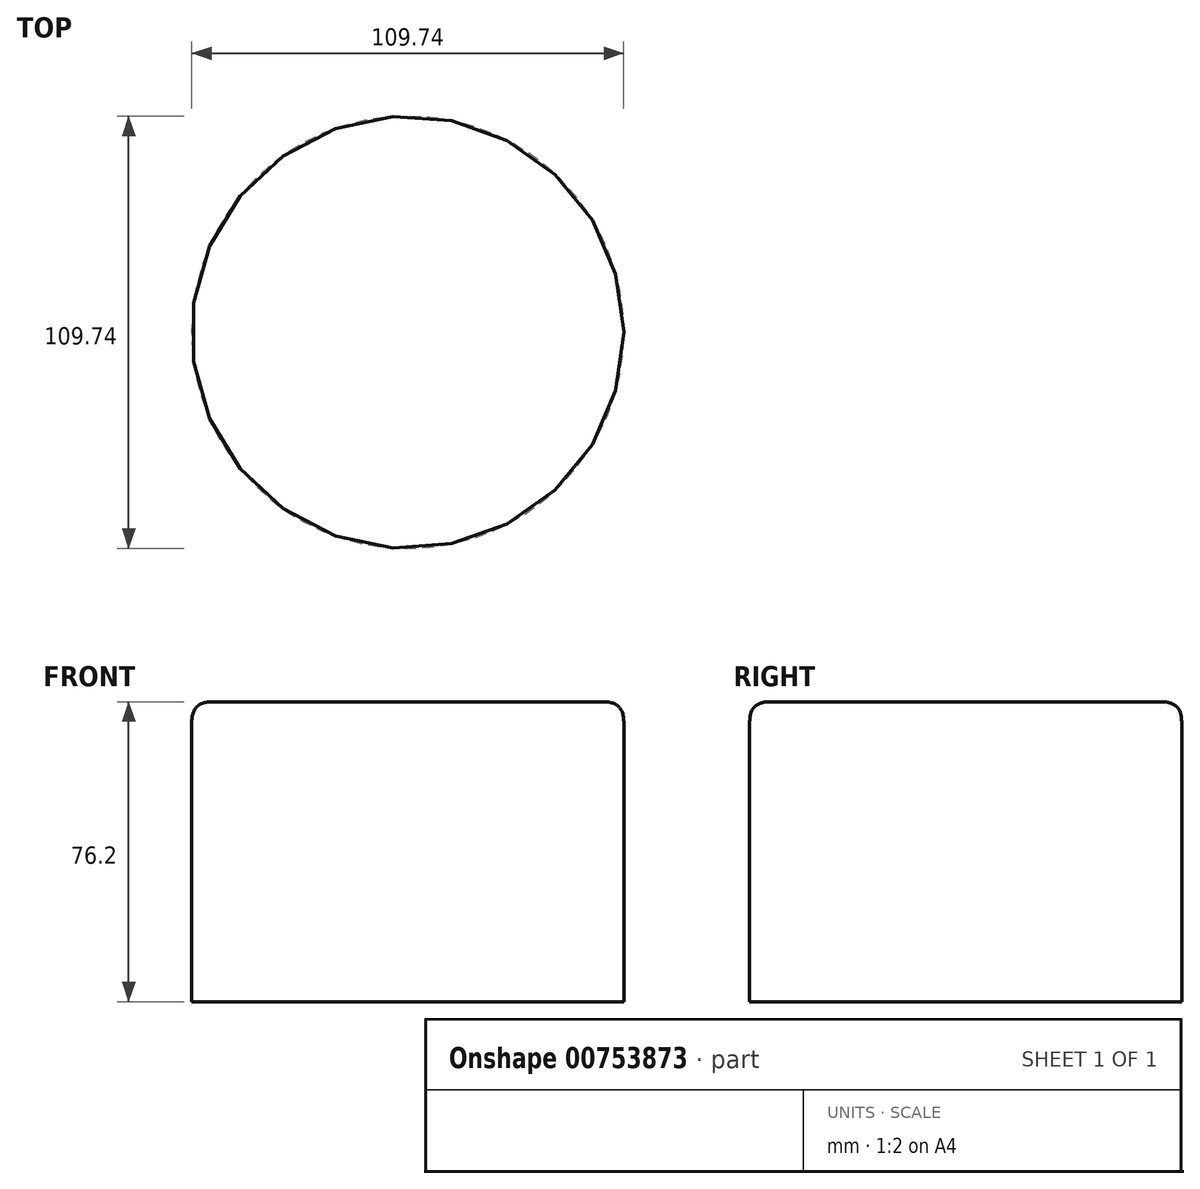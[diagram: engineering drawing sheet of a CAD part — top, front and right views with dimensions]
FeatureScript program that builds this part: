
annotation { "Feature Type Name" : "Feature", "Feature Type Description" : "" }
export const myFeature = defineFeature(function(context is Context, id is Id, definition is map)
    precondition{}
    {
        {
            var Q0;
            Q0=qCreatedBy(makeId("Top.planeOp"),FACE);
            var sketch = newSketch(context, id + "F0", { "sketchPlane" : qUnion([Q0])});
            skCircle(sketch, "E0", {"center": v(0, 0) * mm, "radius": 54.87 * mm});
            skSolve(sketch);
        }
        {
            var Q0;
            Q0=makeQuery(id+"F0.imprint","IMPRINT",FACE,{"disambiguationData":[TD([[makeQuery(id+"F0.imprint","IMPRINT",EDGE,{"derivedFrom":sQuery(id+"F0.wireOp",EDGE,"E0")}),1.0]])]});
            extrude(context, id + "F1", {"entities" : qUnion([Q0]), "depth" : 76.2 * mm, "offsetDistance" : 25.4 * mm});
        }
        {
            var Q0;
            Q0=makeQuery(id+"F1.opExtrude","CAP_EDGE",EDGE,{"disambiguationData":[OSD([sQuery(id+"F0.wireOp",EDGE,"E0")])],"isStart":false});
            fillet(context, id + "F2", {"entities" : qUnion([Q0]), "radius" : 5.08 * mm, "tangentPropagation" : true, "rho" : 0.5, "crossSection" : FilletCrossSection.CONIC, "allowEdgeOverflow" : false});
        }
    });
